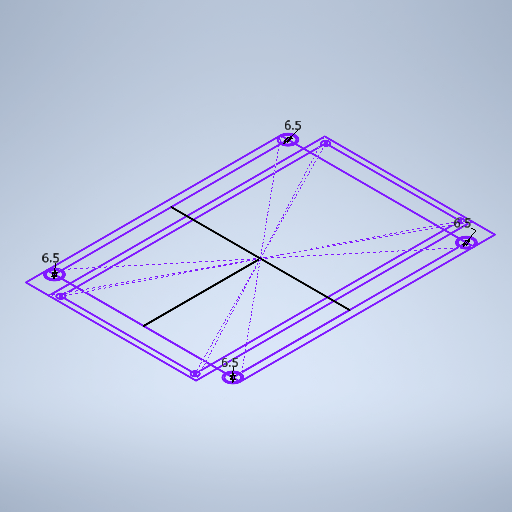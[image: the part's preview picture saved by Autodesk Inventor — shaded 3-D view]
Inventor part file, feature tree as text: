
AUTODESK INVENTOR PART (.ipt)
format: ipt  version: 2025 (Build 290162000, 162)  size: 260,608 bytes
history: native  units: mm
features: sketch x1
ambient origin geometry x8: Origin, YZ Plane, XZ Plane, XY Plane, X Axis, Y Axis, Z Axis, Center Point
feature tree (1):
  sketch  "Sketch1"  dims[d14=6.5mm d15=6.5mm d16=6.5mm d17=6.5mm]
